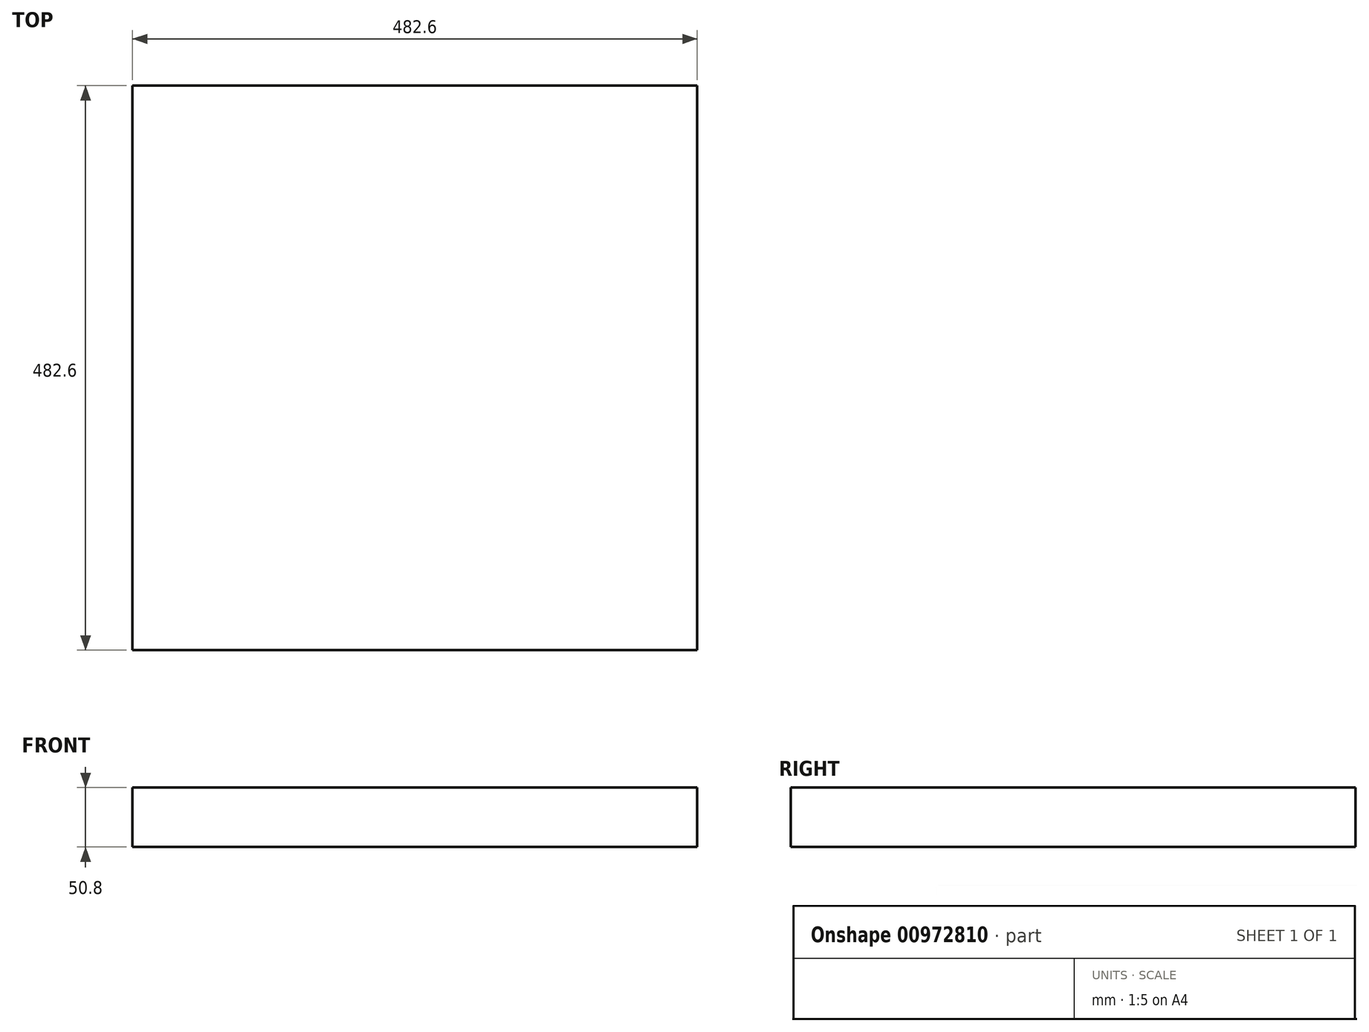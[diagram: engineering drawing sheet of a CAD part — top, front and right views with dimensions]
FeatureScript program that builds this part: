
annotation { "Feature Type Name" : "Feature", "Feature Type Description" : "" }
export const myFeature = defineFeature(function(context is Context, id is Id, definition is map)
    precondition{}
    {
        {
            var Q0;
            Q0=qCreatedBy(makeId("Top.planeOp"),FACE);
            var sketch = newSketch(context, id + "F0", { "sketchPlane" : qUnion([Q0])});
            skLineSegment(sketch, "E0.bottom", {"start": v(241.3, 241.3) * mm, "end": v(-241.3, 241.3) * mm});
            skLineSegment(sketch, "E0.top", {"start": v(241.3, -241.3) * mm, "end": v(-241.3, -241.3) * mm});
            skLineSegment(sketch, "E0.left", {"start": v(241.3, 241.3) * mm, "end": v(241.3, -241.3) * mm});
            skLineSegment(sketch, "E0.right", {"start": v(-241.3, 241.3) * mm, "end": v(-241.3, -241.3) * mm});
            skPoint(sketch, "E0.middle", {"position": v(0, 0) * mm});
            skSolve(sketch);
        }
        {
            var Q0;
            Q0=makeQuery(id+"F0.imprint","IMPRINT",FACE,{"disambiguationData":[TD([[makeQuery(id+"F0.imprint","IMPRINT",EDGE,{"derivedFrom":sQuery(id+"F0.wireOp",EDGE,"E0.bottom")}),1.0]])]});
            extrude(context, id + "F1", {"entities" : qUnion([Q0]), "depth" : 50.8 * mm, "offsetDistance" : 25.4 * mm});
        }
    });
